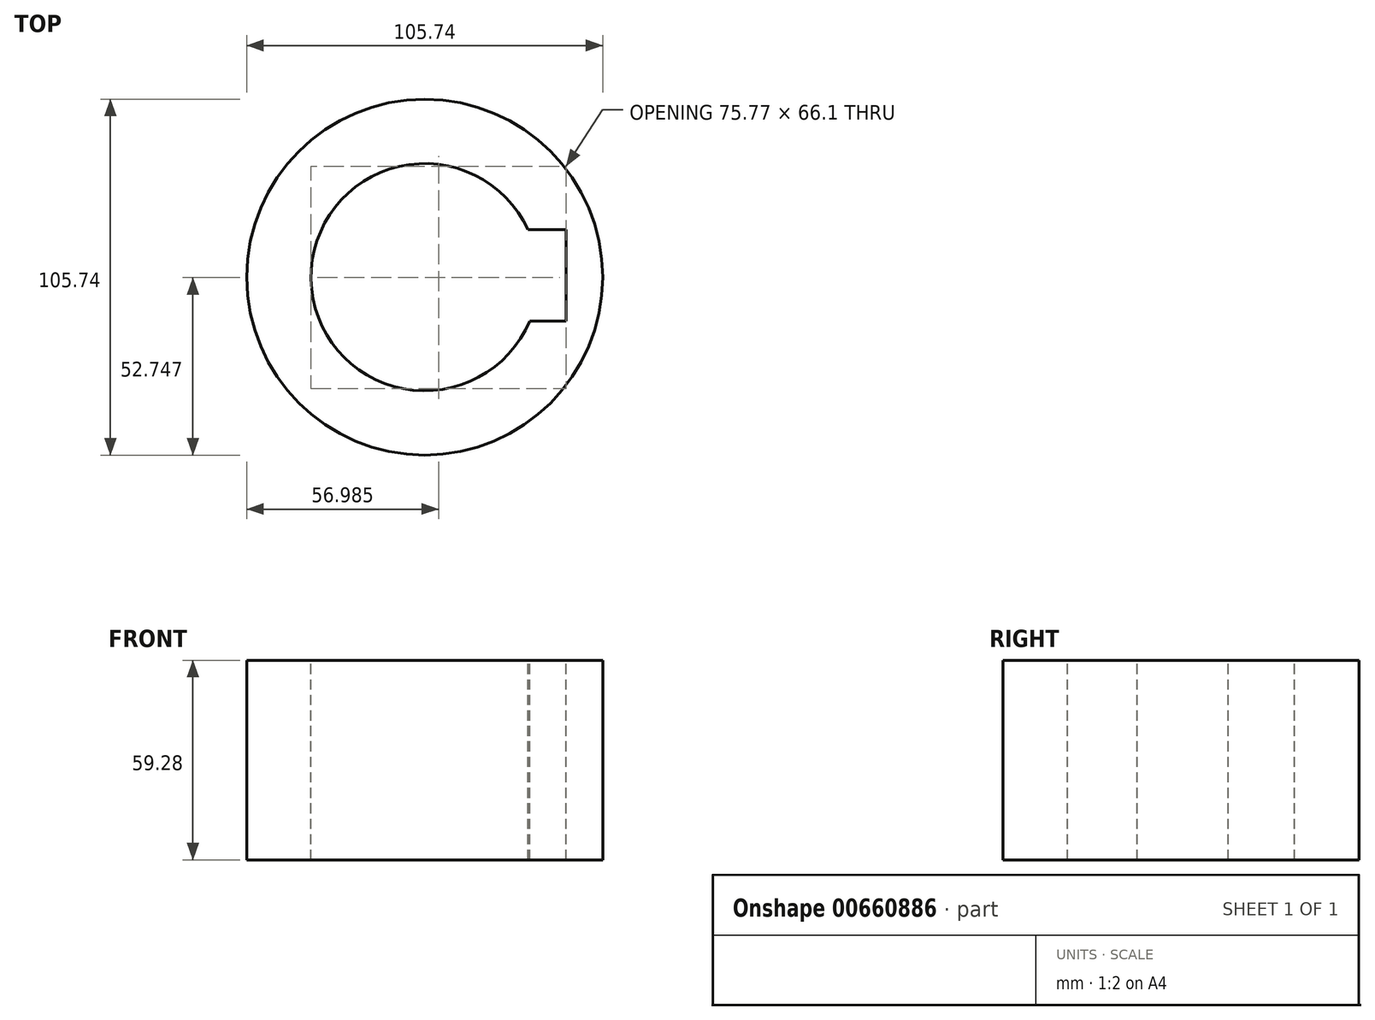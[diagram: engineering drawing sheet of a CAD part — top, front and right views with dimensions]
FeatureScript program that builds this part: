
annotation { "Feature Type Name" : "Feature", "Feature Type Description" : "" }
export const myFeature = defineFeature(function(context is Context, id is Id, definition is map)
    precondition{}
    {
        {
            var Q0;
            Q0=qCreatedBy(makeId("Front.planeOp"),FACE);
            var sketch = newSketch(context, id + "F0", { "sketchPlane" : qUnion([Q0])});
            skLineSegment(sketch, "E0", {"start": v(-56.93, -21.74) * mm, "end": v(-56.93, 37.6) * mm});
            skLineSegment(sketch, "E1", {"start": v(0, 67.28) * mm, "end": v(0, -73.21) * mm, "construction": true});
            skSolve(sketch);
        }
        {
            var Q0;
            Q0=qCreatedBy(makeId("Front.planeOp"),FACE);
            var sketch = newSketch(context, id + "F1", { "sketchPlane" : qUnion([Q0])});
            skLineSegment(sketch, "E2", {"start": v(-33.77, 36.55) * mm, "end": v(-52.87, 36.55) * mm});
            skLineSegment(sketch, "E3", {"start": v(-52.87, 36.55) * mm, "end": v(-52.87, -22.8) * mm});
            skLineSegment(sketch, "E4", {"start": v(-54.74, -22.73) * mm, "end": v(-33.77, -22.73) * mm});
            skLineSegment(sketch, "E5", {"start": v(-33.77, -22.73) * mm, "end": v(-33.77, 36.55) * mm});
            skSolve(sketch);
        }
        {
            var Q0;
            Q0 = qSketchRegion(id + "F1", true);
            var Q1;
            Q1=sQuery(id+"F0.wireOp",EDGE,"E1");
            revolve(context, id + "F2", {"entities" : qUnion([Q0]), "axis" : qUnion([Q1]), "revolveType" : RevolveType.FULL});
        }
        {
            var Q0;
            Q0=makeQuery(id+"F2.opRevolve","SWEPT_FACE",FACE,{"disambiguationData":[OSD([sQuery(id+"F1.wireOp",EDGE,"E2")])]});
            var sketch = newSketch(context, id + "F3", { "sketchPlane" : qUnion([Q0])});
            skLineSegment(sketch, "E6.bottom", {"start": v(12.88, 14.1) * mm, "end": v(42, 14.1) * mm});
            skLineSegment(sketch, "E6.top", {"start": v(12.88, -13) * mm, "end": v(42, -13) * mm});
            skLineSegment(sketch, "E6.left", {"start": v(12.88, 14.1) * mm, "end": v(12.88, -13) * mm});
            skLineSegment(sketch, "E6.right", {"start": v(42, 14.1) * mm, "end": v(42, -13) * mm});
            skSolve(sketch);
        }
        {
            var Q0;
            Q0 = qSketchRegion(id + "F3", true);
            extrude(context, id + "F4", {"entities" : qUnion([Q0]), "operationType" : NewBodyOperationType.REMOVE, "oppositeDirection" : true, "depth" : 76.2 * mm, "offsetDistance" : 25.4 * mm});
        }
        {
            var Q0;
            Q0=qCreatedBy(makeId("Front.planeOp"),FACE);
            var sketch = newSketch(context, id + "F5", { "sketchPlane" : qUnion([Q0])});
            skCircle(sketch, "E7", {"center": v(0, 0) * mm, "radius": 12.7 * mm});
            skSolve(sketch);
        }
        {
            var Q0;
            Q0 = qSketchRegion(id + "F5", true);
            extrude(context, id + "F6", {"entities" : qUnion([Q0]), "operationType" : NewBodyOperationType.REMOVE, "endBound" : BoundingType.SYMMETRIC, "oppositeDirection" : true, "depth" : 25.4 * mm, "offsetDistance" : 25.4 * mm});
        }
    });
